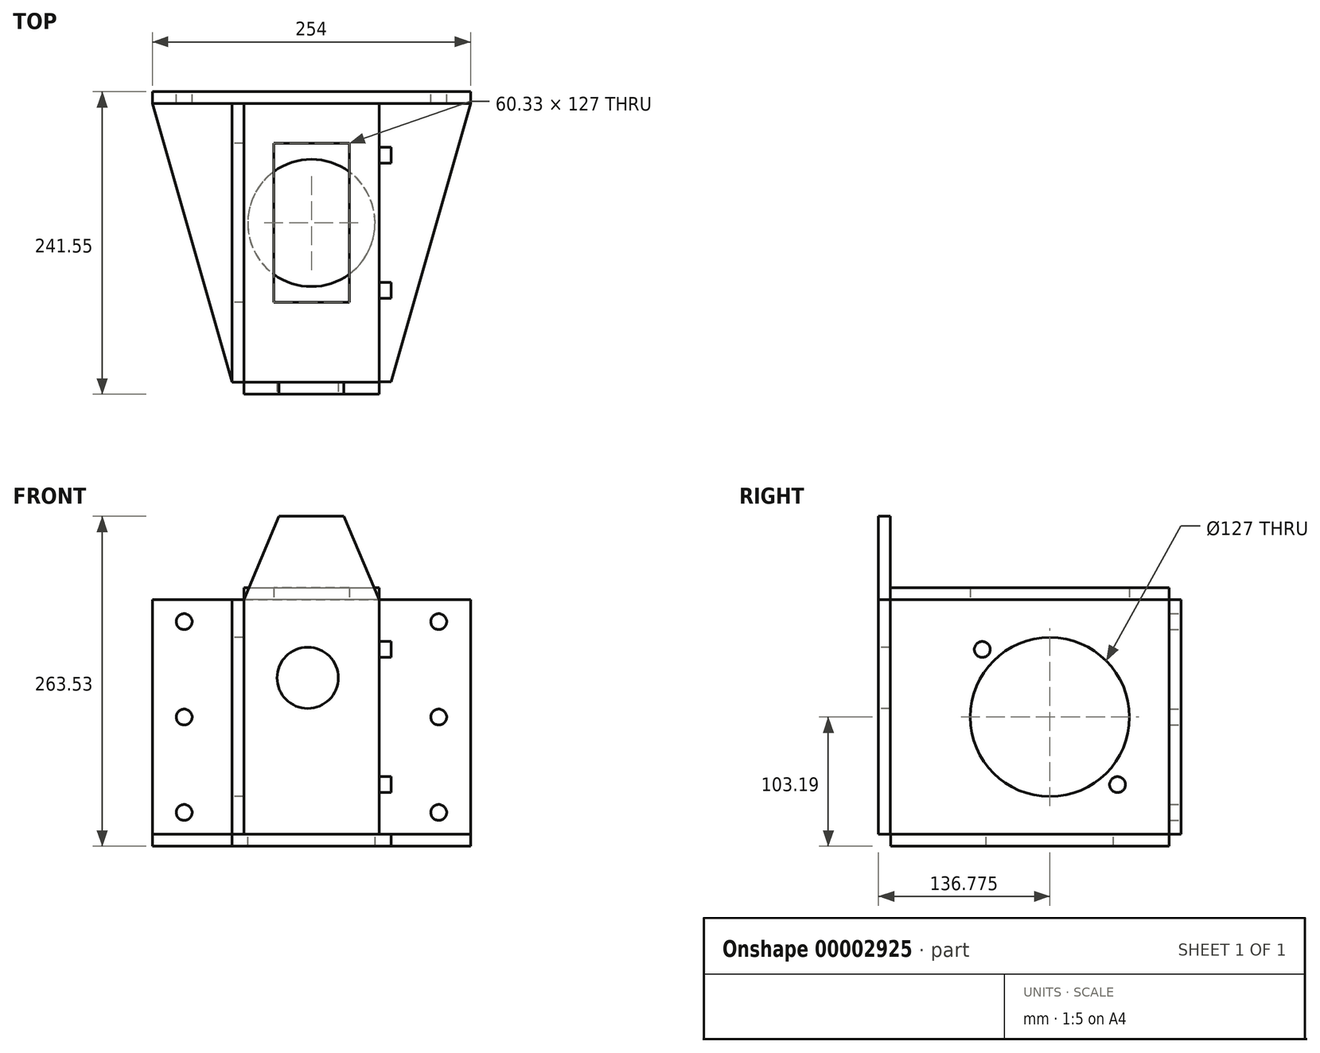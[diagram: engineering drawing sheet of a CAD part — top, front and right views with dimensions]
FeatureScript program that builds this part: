
annotation { "Feature Type Name" : "Feature", "Feature Type Description" : "" }
export const myFeature = defineFeature(function(context is Context, id is Id, definition is map)
    precondition{}
    {
        {
            var Q0;
            Q0=qCreatedBy(makeId("Front.planeOp"),FACE);
            var sketch = newSketch(context, id + "F0", { "sketchPlane" : qUnion([Q0])});
            skLineSegment(sketch, "E0.rect.bottom", {"start": v(127, -93.66) * mm, "end": v(-127, -93.66) * mm});
            skLineSegment(sketch, "E0.rect.top", {"start": v(127, 93.66) * mm, "end": v(-127, 93.66) * mm});
            skLineSegment(sketch, "E0.rect.left", {"start": v(127, -93.66) * mm, "end": v(127, 93.66) * mm});
            skLineSegment(sketch, "E0.rect.right", {"start": v(-127, -93.66) * mm, "end": v(-127, 93.66) * mm});
            skPoint(sketch, "E0.rect.middle", {"position": v(0, 0) * mm});
            skLineSegment(sketch, "E1", {"start": v(-101.6, 93.66) * mm, "end": v(-101.6, -93.66) * mm, "construction": true});
            skCircle(sketch, "E2", {"center": v(-101.6, 0) * mm, "radius": 6.35 * mm});
            skCircle(sketch, "E3", {"center": v(-101.6, 76.2) * mm, "radius": 6.35 * mm});
            skCircle(sketch, "E4", {"center": v(-101.6, -76.2) * mm, "radius": 6.35 * mm});
            skLineSegment(sketch, "E5", {"start": v(0, 0) * mm, "end": v(0, 93.66) * mm, "construction": true});
            skCircle(sketch, "E6.0.MirrorC", {"center": v(101.6, 76.2) * mm, "radius": 6.35 * mm});
            skCircle(sketch, "E7.0.MirrorC", {"center": v(101.6, 0) * mm, "radius": 6.35 * mm});
            skCircle(sketch, "E8.0.MirrorC", {"center": v(101.6, -76.2) * mm, "radius": 6.35 * mm});
            skSolve(sketch);
        }
        {
            var Q0;
            Q0=makeQuery(id+"F0.imprint","IMPRINT",FACE,{"disambiguationData":[TD([[makeQuery(id+"F0.imprint","IMPRINT",EDGE,{"derivedFrom":sQuery(id+"F0.wireOp",EDGE,"E0.rect.bottom")}),-1.0]])]});
            extrude(context, id + "F1", {"entities" : qUnion([Q0]), "depth" : 9.52 * mm});
        }
        {
            var Q0;
            Q0=makeQuery(id+"F1.opExtrude","SWEPT_FACE",FACE,{"disambiguationData":[OSD([sQuery(id+"F0.wireOp",EDGE,"E0.rect.bottom")])]});
            var sketch = newSketch(context, id + "F2", { "sketchPlane" : qUnion([Q0])});
            skLineSegment(sketch, "E9", {"start": v(-127, 0) * mm, "end": v(-63.5, -222.25) * mm});
            skLineSegment(sketch, "E10", {"start": v(-63.5, -222.25) * mm, "end": v(63.5, -222.25) * mm});
            skLineSegment(sketch, "E11", {"start": v(63.5, -222.25) * mm, "end": v(127, 0) * mm});
            skLineSegment(sketch, "E12", {"start": v(0, 0) * mm, "end": v(0, -222.25) * mm, "construction": true});
            skCircle(sketch, "E13", {"center": v(0, -95.25) * mm, "radius": 50.8 * mm});
            skSolve(sketch);
        }
        {
            var Q0;
            Q0=makeQuery(id+"F2.imprint","IMPRINT",FACE,{"disambiguationData":[TD([[makeQuery(id+"F2.imprint","IMPRINT",EDGE,{"derivedFrom":sQuery(id+"F2.wireOp",EDGE,"E9")}),1.0]])]});
            extrude(context, id + "F3", {"entities" : qUnion([Q0]), "depth" : 9.52 * mm});
        }
        {
            var Q0;
            Q0=makeQuery(id+"F1.opExtrude","CAP_FACE",FACE,{"disambiguationData":[OSD([sQuery(id+"F0.wireOp",EDGE,"E0.rect.bottom"),sQuery(id+"F0.wireOp",EDGE,"E0.rect.top"),sQuery(id+"F0.wireOp",EDGE,"E0.rect.left"),sQuery(id+"F0.wireOp",EDGE,"E0.rect.right"),sQuery(id+"F0.wireOp",EDGE,"E2"),sQuery(id+"F0.wireOp",EDGE,"E3"),sQuery(id+"F0.wireOp",EDGE,"E4"),sQuery(id+"F0.wireOp",EDGE,"E6.0.MirrorC"),sQuery(id+"F0.wireOp",EDGE,"E7.0.MirrorC"),sQuery(id+"F0.wireOp",EDGE,"E8.0.MirrorC")])],"isStart":false});
            var Q1;
            Q1=makeQuery(id+"F1.opExtrude","CAP_FACE",FACE,{"disambiguationData":[OSD([sQuery(id+"F0.wireOp",EDGE,"E0.rect.bottom"),sQuery(id+"F0.wireOp",EDGE,"E0.rect.top"),sQuery(id+"F0.wireOp",EDGE,"E0.rect.left"),sQuery(id+"F0.wireOp",EDGE,"E0.rect.right"),sQuery(id+"F0.wireOp",EDGE,"E2"),sQuery(id+"F0.wireOp",EDGE,"E3"),sQuery(id+"F0.wireOp",EDGE,"E4"),sQuery(id+"F0.wireOp",EDGE,"E6.0.MirrorC"),sQuery(id+"F0.wireOp",EDGE,"E7.0.MirrorC"),sQuery(id+"F0.wireOp",EDGE,"E8.0.MirrorC")])],"isStart":true});
            cPlane(context, id + "F4", {"entities" : qUnion([Q0, Q1]), "cplaneType" : CPlaneType.MID_PLANE, "offset" : 152.4 * mm, "width" : 152.4 * mm, "height" : 152.4 * mm});
        }
        {
            var Q0;
            Q0=makeQuery(id+"F3.opExtrude","SWEPT_BODY",BODY,{"disambiguationData":[OSD([sQuery(id+"F0.wireOp",EDGE,"E0.rect.bottom"),sQuery(id+"F2.wireOp",EDGE,"E9"),sQuery(id+"F2.wireOp",EDGE,"E10"),sQuery(id+"F2.wireOp",EDGE,"E11"),sQuery(id+"F2.wireOp",EDGE,"E13")])]});
            var Q1;
            Q1=qCreatedBy(id+"F4.planeOp",FACE);
            mirror(context, id + "F5", {"entities" : qUnion([Q0]), "mirrorPlane" : qUnion([Q1])});
        }
        {
            var Q0;
            Q0=makeQuery(id+"F3.opExtrude","SWEPT_BODY",BODY,{"disambiguationData":[OSD([sQuery(id+"F0.wireOp",EDGE,"E0.rect.bottom"),sQuery(id+"F2.wireOp",EDGE,"E9"),sQuery(id+"F2.wireOp",EDGE,"E10"),sQuery(id+"F2.wireOp",EDGE,"E11"),sQuery(id+"F2.wireOp",EDGE,"E13")])]});
            deleteBodies(context, id + "F6", {"entities" : qUnion([Q0])});
        }
        {
            var Q0;
            Q0=makeQuery(id+"F1.opExtrude","CAP_FACE",FACE,{"disambiguationData":[OSD([sQuery(id+"F0.wireOp",EDGE,"E0.rect.bottom"),sQuery(id+"F0.wireOp",EDGE,"E0.rect.top"),sQuery(id+"F0.wireOp",EDGE,"E0.rect.left"),sQuery(id+"F0.wireOp",EDGE,"E0.rect.right"),sQuery(id+"F0.wireOp",EDGE,"E2"),sQuery(id+"F0.wireOp",EDGE,"E3"),sQuery(id+"F0.wireOp",EDGE,"E4"),sQuery(id+"F0.wireOp",EDGE,"E6.0.MirrorC"),sQuery(id+"F0.wireOp",EDGE,"E7.0.MirrorC"),sQuery(id+"F0.wireOp",EDGE,"E8.0.MirrorC")])],"isStart":false});
            var sketch = newSketch(context, id + "F7", { "sketchPlane" : qUnion([Q0])});
            skLineSegment(sketch, "E14", {"start": v(0, 93.66) * mm, "end": v(0, -93.66) * mm, "construction": true});
            skLineSegment(sketch, "E15.bottom", {"start": v(-53.98, 93.66) * mm, "end": v(-63.5, 93.66) * mm});
            skLineSegment(sketch, "E15.top", {"start": v(-53.97, -93.66) * mm, "end": v(-63.5, -93.66) * mm});
            skLineSegment(sketch, "E15.left", {"start": v(-53.98, 93.66) * mm, "end": v(-53.97, -93.66) * mm});
            skLineSegment(sketch, "E15.right", {"start": v(-63.5, 93.66) * mm, "end": v(-63.5, -93.66) * mm});
            skLineSegment(sketch, "E16.0.MirrorCS", {"start": v(53.97, 93.66) * mm, "end": v(53.98, -93.66) * mm});
            skLineSegment(sketch, "E16.1.MirrorCS", {"start": v(63.5, 93.66) * mm, "end": v(63.5, -93.66) * mm});
            skLineSegment(sketch, "E16.2.MirrorCS", {"start": v(53.97, 93.66) * mm, "end": v(63.5, 93.66) * mm});
            skLineSegment(sketch, "E16.3.MirrorCS", {"start": v(53.98, -93.66) * mm, "end": v(63.5, -93.66) * mm});
            skSolve(sketch);
        }
        {
            var Q0;
            Q0=makeQuery(id+"F7.imprint","IMPRINT",FACE,{"disambiguationData":[TD([[makeQuery(id+"F7.imprint","IMPRINT",EDGE,{"derivedFrom":sQuery(id+"F7.wireOp",EDGE,"E15.bottom")}),1.0]])]});
            var Q1;
            Q1=makeQuery(id+"F7.imprint","IMPRINT",FACE,{"disambiguationData":[TD([[makeQuery(id+"F7.imprint","IMPRINT",EDGE,{"derivedFrom":sQuery(id+"F7.wireOp",EDGE,"E16.0.MirrorCS")}),1.0]])]});
            extrude(context, id + "F8", {"entities" : qUnion([Q0, Q1]), "depth" : 222.5 * mm});
        }
        {
            var Q0;
            Q0=makeQuery(id+"F8.opExtrude","SWEPT_FACE",FACE,{"disambiguationData":[OSD([sQuery(id+"F7.wireOp",EDGE,"E16.1.MirrorCS")])]});
            var sketch = newSketch(context, id + "F9", { "sketchPlane" : qUnion([Q0])});
            skLineSegment(sketch, "E17", {"start": v(-232.03, 0) * mm, "end": v(-9.53, 0) * mm, "construction": true});
            skCircle(sketch, "E18", {"center": v(-104.78, 0) * mm, "radius": 63.5 * mm});
            skLineSegment(sketch, "E19", {"start": v(-104.78, 0) * mm, "end": v(-104.78, -97.65) * mm, "construction": true});
            skCircle(sketch, "E20", {"center": v(-158.75, -53.98) * mm, "radius": 6.35 * mm});
            skCircle(sketch, "E21.0.MirrorC", {"center": v(-50.8, -53.98) * mm, "radius": 6.35 * mm});
            skCircle(sketch, "E22.0.MirrorC", {"center": v(-50.8, 53.98) * mm, "radius": 6.35 * mm});
            skCircle(sketch, "E23.0.MirrorC", {"center": v(-158.75, 53.98) * mm, "radius": 6.35 * mm});
            skSolve(sketch);
        }
        {
            var Q0;
            Q0=makeQuery(id+"F9.imprint","IMPRINT",FACE,{"disambiguationData":[TD([[makeQuery(id+"F9.imprint","IMPRINT",EDGE,{"derivedFrom":sQuery(id+"F9.wireOp",EDGE,"E23.0.MirrorC")}),-1.0]])]});
            var Q1;
            Q1=makeQuery(id+"F9.imprint","IMPRINT",FACE,{"disambiguationData":[TD([[makeQuery(id+"F9.imprint","IMPRINT",EDGE,{"derivedFrom":sQuery(id+"F9.wireOp",EDGE,"E18")}),1.0]])]});
            var Q2;
            Q2=makeQuery(id+"F9.imprint","IMPRINT",FACE,{"disambiguationData":[TD([[makeQuery(id+"F9.imprint","IMPRINT",EDGE,{"derivedFrom":sQuery(id+"F9.wireOp",EDGE,"E22.0.MirrorC")}),1.0]])]});
            var Q3;
            Q3=makeQuery(id+"F9.imprint","IMPRINT",FACE,{"disambiguationData":[TD([[makeQuery(id+"F9.imprint","IMPRINT",EDGE,{"derivedFrom":sQuery(id+"F9.wireOp",EDGE,"E21.0.MirrorC")}),-1.0]])]});
            var Q4;
            Q4=makeQuery(id+"F9.imprint","IMPRINT",FACE,{"disambiguationData":[TD([[makeQuery(id+"F9.imprint","IMPRINT",EDGE,{"derivedFrom":sQuery(id+"F9.wireOp",EDGE,"E20")}),1.0]])]});
            extrude(context, id + "F10", {"entities" : qUnion([Q0, Q1, Q2, Q3, Q4]), "operationType" : NewBodyOperationType.REMOVE, "oppositeDirection" : true, "depth" : 25.4 * mm});
        }
        {
            var Q0;
            Q0=makeQuery(id+"F8.opExtrude","SWEPT_FACE",FACE,{"disambiguationData":[OSD([sQuery(id+"F7.wireOp",EDGE,"E15.right")])]});
            var sketch = newSketch(context, id + "F11", { "sketchPlane" : qUnion([Q0])});
            skCircle(sketch, "E24", {"center": v(104.78, 0) * mm, "radius": 63.5 * mm});
            skSolve(sketch);
        }
        {
            var Q0;
            Q0=makeQuery(id+"F11.imprint","IMPRINT",FACE,{"disambiguationData":[TD([[makeQuery(id+"F11.imprint","IMPRINT",EDGE,{"derivedFrom":sQuery(id+"F11.wireOp",EDGE,"E24")}),1.0]])]});
            extrude(context, id + "F12", {"entities" : qUnion([Q0]), "operationType" : NewBodyOperationType.REMOVE, "oppositeDirection" : true, "depth" : 25.4 * mm});
        }
        {
            var Q0;
            Q0=makeQuery(id+"F8.opExtrude","CAP_FACE",FACE,{"disambiguationData":[OSD([sQuery(id+"F7.wireOp",EDGE,"E15.bottom"),sQuery(id+"F7.wireOp",EDGE,"E15.top"),sQuery(id+"F7.wireOp",EDGE,"E15.left"),sQuery(id+"F7.wireOp",EDGE,"E15.right")])],"isStart":false});
            var sketch = newSketch(context, id + "F13", { "sketchPlane" : qUnion([Q0])});
            skLineSegment(sketch, "E25", {"start": v(-53.98, -93.66) * mm, "end": v(-53.98, 93.66) * mm});
            skLineSegment(sketch, "E26", {"start": v(-53.97, 93.66) * mm, "end": v(-25.88, 160.34) * mm});
            skLineSegment(sketch, "E27", {"start": v(-25.88, 160.34) * mm, "end": v(25.88, 160.34) * mm});
            skLineSegment(sketch, "E28", {"start": v(25.88, 160.34) * mm, "end": v(53.97, 93.66) * mm});
            skLineSegment(sketch, "E29", {"start": v(53.97, 93.66) * mm, "end": v(53.98, -93.66) * mm});
            skLineSegment(sketch, "E30", {"start": v(-53.97, 93.66) * mm, "end": v(53.97, 93.66) * mm});
            skLineSegment(sketch, "E31", {"start": v(0, 93.66) * mm, "end": v(0, 160.34) * mm});
            skLineSegment(sketch, "E32", {"start": v(-53.98, -93.66) * mm, "end": v(53.98, -93.66) * mm});
            skSolve(sketch);
        }
        {
            var Q0;
            {var subQ2=sQuery(id+"F13.wireOp",EDGE,"E26");Q0=makeQuery(id+"F13.imprint","IMPRINT",FACE,{"disambiguationData":[TD([[makeQuery(id+"F13.imprint","IMPRINT",EDGE,{"derivedFrom":subQ2}),-1.0]])]});}
            var Q1;
            {var subQ2=sQuery(id+"F13.wireOp",EDGE,"E28");Q1=makeQuery(id+"F13.imprint","IMPRINT",FACE,{"disambiguationData":[TD([[makeQuery(id+"F13.imprint","IMPRINT",EDGE,{"derivedFrom":subQ2}),-1.0]])]});}
            var Q2;
            {var subQ3=sQuery(id+"F13.wireOp",EDGE,"E25");Q2=makeQuery(id+"F13.imprint","IMPRINT",FACE,{"disambiguationData":[TD([[makeQuery(id+"F13.imprint","IMPRINT",EDGE,{"derivedFrom":subQ3}),1.0]])]});}
            extrude(context, id + "F14", {"entities" : qUnion([Q0, Q1, Q2]), "depth" : 9.52 * mm});
        }
        {
            var Q0;
            Q0=makeQuery(id+"F8.opExtrude","SWEPT_FACE",FACE,{"disambiguationData":[OSD([sQuery(id+"F7.wireOp",EDGE,"E15.bottom")])]});
            var sketch = newSketch(context, id + "F15", { "sketchPlane" : qUnion([Q0])});
            skLineSegment(sketch, "E33.bottom", {"start": v(-53.97, -9.53) * mm, "end": v(53.97, -9.53) * mm});
            skLineSegment(sketch, "E33.top", {"start": v(-53.97, -232.03) * mm, "end": v(53.97, -232.03) * mm});
            skLineSegment(sketch, "E33.left", {"start": v(-53.97, -9.53) * mm, "end": v(-53.97, -232.03) * mm});
            skLineSegment(sketch, "E33.right", {"start": v(53.97, -9.53) * mm, "end": v(53.98, -232.03) * mm});
            skLineSegment(sketch, "E34", {"start": v(0, -232.03) * mm, "end": v(0, -9.53) * mm, "construction": true});
            skLineSegment(sketch, "E35.rect.bottom", {"start": v(30.16, -41.27) * mm, "end": v(-30.16, -41.27) * mm});
            skLineSegment(sketch, "E35.rect.top", {"start": v(30.16, -168.28) * mm, "end": v(-30.16, -168.28) * mm});
            skLineSegment(sketch, "E35.rect.left", {"start": v(30.16, -41.27) * mm, "end": v(30.16, -168.27) * mm});
            skLineSegment(sketch, "E35.rect.right", {"start": v(-30.16, -41.27) * mm, "end": v(-30.16, -168.28) * mm});
            skPoint(sketch, "E35.rect.middle", {"position": v(0, -104.77) * mm});
            skSolve(sketch);
        }
        {
            var Q0;
            Q0=makeQuery(id+"F15.imprint","IMPRINT",FACE,{"disambiguationData":[TD([[makeQuery(id+"F15.imprint","IMPRINT",EDGE,{"derivedFrom":sQuery(id+"F15.wireOp",EDGE,"E33.bottom")}),-1.0]])]});
            extrude(context, id + "F16", {"entities" : qUnion([Q0]), "depth" : 9.52 * mm});
        }
        {
            var Q0;
            Q0=makeQuery(id+"F14.opExtrude","CAP_FACE",FACE,{"disambiguationData":[OSD([sQuery(id+"F13.wireOp",EDGE,"E25"),sQuery(id+"F13.wireOp",EDGE,"E26"),sQuery(id+"F13.wireOp",EDGE,"E27"),sQuery(id+"F13.wireOp",EDGE,"E28"),sQuery(id+"F13.wireOp",EDGE,"E29"),sQuery(id+"F13.wireOp",EDGE,"E32")])],"isStart":false});
            var sketch = newSketch(context, id + "F17", { "sketchPlane" : qUnion([Q0])});
            skCircle(sketch, "E36", {"center": v(-2.97, 31.37) * mm, "radius": 24.46 * mm});
            skSolve(sketch);
        }
        {
            var Q0;
            Q0=makeQuery(id+"F17.imprint","IMPRINT",FACE,{"disambiguationData":[TD([[makeQuery(id+"F17.imprint","IMPRINT",EDGE,{"derivedFrom":sQuery(id+"F17.wireOp",EDGE,"E36")}),1.0]])]});
            extrude(context, id + "F18", {"entities" : qUnion([Q0]), "operationType" : NewBodyOperationType.REMOVE, "oppositeDirection" : true, "depth" : 25.4 * mm});
        }
    });
